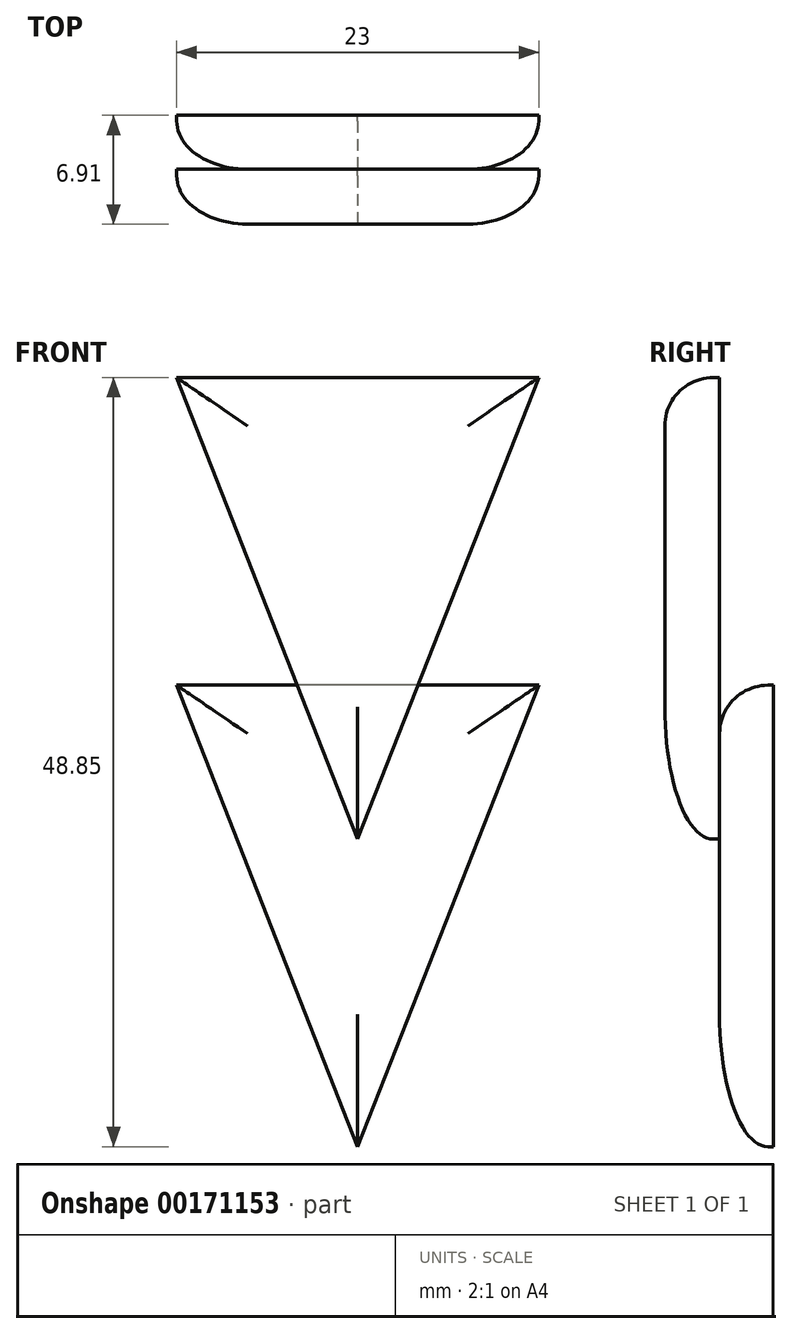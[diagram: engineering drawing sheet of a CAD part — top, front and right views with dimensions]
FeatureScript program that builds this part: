
annotation { "Feature Type Name" : "Feature", "Feature Type Description" : "" }
export const myFeature = defineFeature(function(context is Context, id is Id, definition is map)
    precondition{}
    {
        {
            var Q0;
            Q0=qCreatedBy(makeId("Front.planeOp"),FACE);
            var sketch = newSketch(context, id + "F0", { "sketchPlane" : qUnion([Q0])});
            skLineSegment(sketch, "E0", {"start": v(-11.5, 29.3) * mm, "end": v(0, 0) * mm});
            skLineSegment(sketch, "E1", {"start": v(0, 0) * mm, "end": v(11.5, 29.3) * mm});
            skLineSegment(sketch, "E2", {"start": v(11.5, 29.3) * mm, "end": v(-11.5, 29.3) * mm});
            skSolve(sketch);
        }
        {
            var Q0;
            Q0=makeQuery(id+"F0.imprint","IMPRINT",FACE,{"disambiguationData":[TD([[makeQuery(id+"F0.imprint","IMPRINT",EDGE,{"derivedFrom":sQuery(id+"F0.wireOp",EDGE,"E0")}),1.0]])]});
            extrude(context, id + "F1", {"entities" : qUnion([Q0]), "depth" : 3.48 * mm});
        }
        {
            var Q0;
            Q0=makeQuery(id+"F1.opExtrude","CAP_FACE",FACE,{"disambiguationData":[OSD([sQuery(id+"F0.wireOp",EDGE,"E0"),sQuery(id+"F0.wireOp",EDGE,"E1"),sQuery(id+"F0.wireOp",EDGE,"E2")])],"isStart":false});
            fillet(context, id + "F2", {"entities" : qUnion([Q0]), "radius" : 3.07 * mm, "tangentPropagation" : true, "allowEdgeOverflow" : false});
        }
        {
            var Q0;
            Q0=qCreatedBy(makeId("Front.planeOp"),FACE);
            cPlane(context, id + "F3", {"entities" : qUnion([Q0]), "cplaneType" : CPlaneType.OFFSET, "offset" : 3.43 * mm, "oppositeDirection" : true, "width" : 152.4 * mm, "height" : 152.4 * mm});
        }
        {
            var Q0;
            Q0=qCreatedBy(id+"F3.planeOp",FACE);
            var sketch = newSketch(context, id + "F4", { "sketchPlane" : qUnion([Q0])});
            skLineSegment(sketch, "E3", {"start": v(-11.5, 9.77) * mm, "end": v(0, -19.54) * mm});
            skLineSegment(sketch, "E4", {"start": v(0, -19.54) * mm, "end": v(11.5, 9.77) * mm});
            skLineSegment(sketch, "E5", {"start": v(11.5, 9.77) * mm, "end": v(-11.5, 9.77) * mm});
            skSolve(sketch);
        }
        {
            var Q0;
            Q0=makeQuery(id+"F4.imprint","IMPRINT",FACE,{"disambiguationData":[TD([[makeQuery(id+"F4.imprint","IMPRINT",EDGE,{"derivedFrom":sQuery(id+"F4.wireOp",EDGE,"E3")}),1.0]])]});
            var Q1;
            Q1=sQuery(id+"F4.wireOp",EDGE,"E3");
            var Q2;
            Q2=sQuery(id+"F4.wireOp",EDGE,"E4");
            var Q3;
            Q3=sQuery(id+"F4.wireOp",EDGE,"E5");
            extrude(context, id + "F5", {"entities" : qUnion([Q0]), "surfaceEntities" : qUnion([Q1, Q2, Q3]), "depth" : 3.43 * mm});
        }
        {
            var Q0;
            Q0=makeQuery(id+"F5.opExtrude","CAP_FACE",FACE,{"disambiguationData":[OSD([sQuery(id+"F4.wireOp",EDGE,"E3"),sQuery(id+"F4.wireOp",EDGE,"E4"),sQuery(id+"F4.wireOp",EDGE,"E5")])],"isStart":false});
            fillet(context, id + "F6", {"entities" : qUnion([Q0]), "radius" : 3.07 * mm, "tangentPropagation" : true, "allowEdgeOverflow" : false});
        }
        {
            var Q0;
            Q0=qCreatedBy(makeId("Top.planeOp"),FACE);
            cPlane(context, id + "F7", {"entities" : qUnion([Q0]), "cplaneType" : CPlaneType.OFFSET, "offset" : 25.4 * mm, "width" : 152.4 * mm, "height" : 152.4 * mm});
        }
    });
